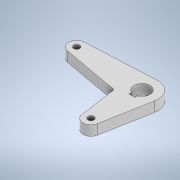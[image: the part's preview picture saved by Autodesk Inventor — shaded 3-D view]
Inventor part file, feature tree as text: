
AUTODESK INVENTOR PART (.ipt)
format: ipt  version: 2021 (Build 250183000, 183)  size: 127,488 bytes
history: native  units: mm
features: extrude x1, sketch x1
ambient origin geometry x8: Origin, YZ Plane, XZ Plane, XY Plane, X Axis, Y Axis, Z Axis, Center Point
bodies: Solid1 (feature_tree)
feature tree (2):
  extrude  "Extrusion1"  Depth=10.0mm
  sketch  "Sketch1"  dims[d0=70.0mm d1=50.0mm d2=8.0mm d3=6.0mm d4=6.0mm d5=8.0mm d6=16.0mm d7=16.0mm d8=18.0mm d9=6.0mm d10=3.0mm d12=2.0mm d13=10.0mm d14=0.0mm]
